# Revit family: LPT
name_source: partatom
category: Lighting Fixtures
revit_build: Autodesk Revit MEP 2012 (Build: 20110916_2132(x64)
units: mm (PartAtom-declared; Revit-internal decimal feet)

## types (2) — shared parameters
Apparent Load = 0 VA
Backbox = White
Color Filter = 16777215
Default Elevation = 4.0'
Description = LPT is available in 4' or 8' lengths with lumen packages ranging from 2,700 to 19,200 nominal.
Dimming Lamp Color Temperature Shift = <None>
Driver = 0-10V Dimming
Emit from Line Length = 2.0'
Glass = White Glass
Lamp = LED Lamp
Manufacturer = Columbia Lighting
Manufacturer Fax = (866)-898-1065
Model = LPT
Product Documentation Link = http://www.columbialighting.com
Product Page URL = http://www.columbialighting.com
Row Length = 4.0'
Tilt Angle = -90.00°
URL = http://www.columbialighting.com
Voltage = 120 V

## per-type parameters (varying)
| type | Lumen Output | Nominal Watts | Photometric Web File |
| LPT4-35ML-EDU | Medium Lumen | 53 W | LPT4-35ML-EDU.ies |
| LPT4-35VL-EDU | Very High Lumen | 105 W | LPT4-35VL-EDU.ies |

## geometry (parser evidence)
native form markers: Sweep x4
no freeform markers — native parametric forms only
